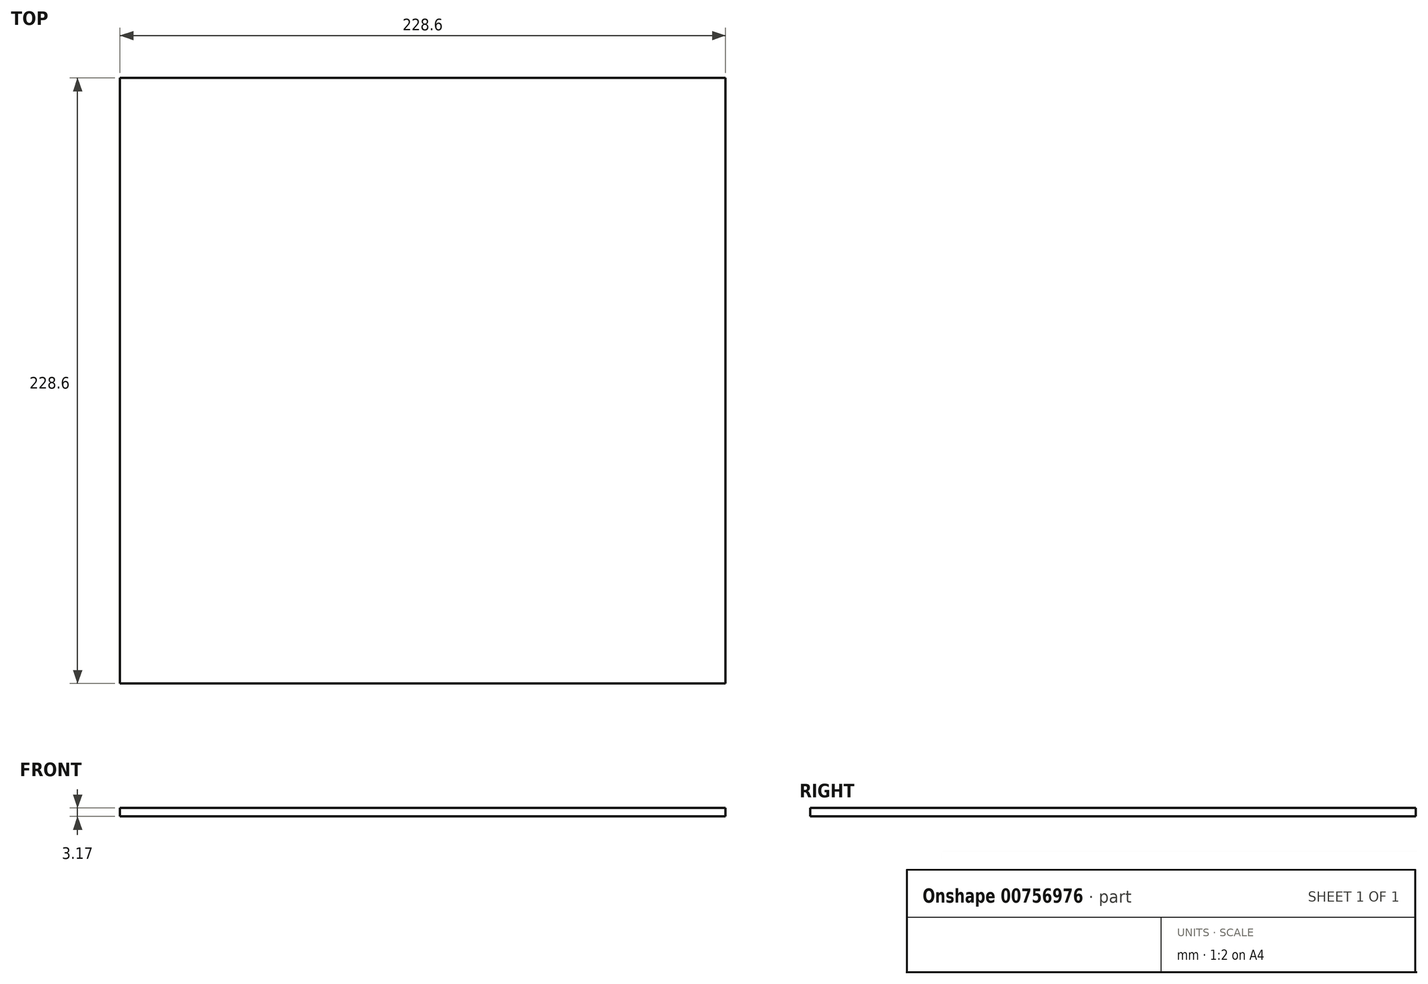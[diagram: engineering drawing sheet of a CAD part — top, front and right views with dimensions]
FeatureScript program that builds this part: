
annotation { "Feature Type Name" : "Feature", "Feature Type Description" : "" }
export const myFeature = defineFeature(function(context is Context, id is Id, definition is map)
    precondition{}
    {
        {
            var Q0;
            Q0=qCreatedBy(makeId("Top.planeOp"),FACE);
            var sketch = newSketch(context, id + "F0", { "sketchPlane" : qUnion([Q0])});
            skLineSegment(sketch, "E0.bottom", {"start": v(114.3, 114.3) * mm, "end": v(-114.3, 114.3) * mm});
            skLineSegment(sketch, "E0.top", {"start": v(114.3, -114.3) * mm, "end": v(-114.3, -114.3) * mm});
            skLineSegment(sketch, "E0.left", {"start": v(114.3, 114.3) * mm, "end": v(114.3, -114.3) * mm});
            skLineSegment(sketch, "E0.right", {"start": v(-114.3, 114.3) * mm, "end": v(-114.3, -114.3) * mm});
            skPoint(sketch, "E0.middle", {"position": v(0, 0) * mm});
            skSolve(sketch);
        }
        {
            var Q0;
            Q0=qSketchRegion(id+"F0",true);
            extrude(context, id + "F1", {"entities" : qUnion([Q0]), "depth" : 3.17 * mm});
        }
    });
